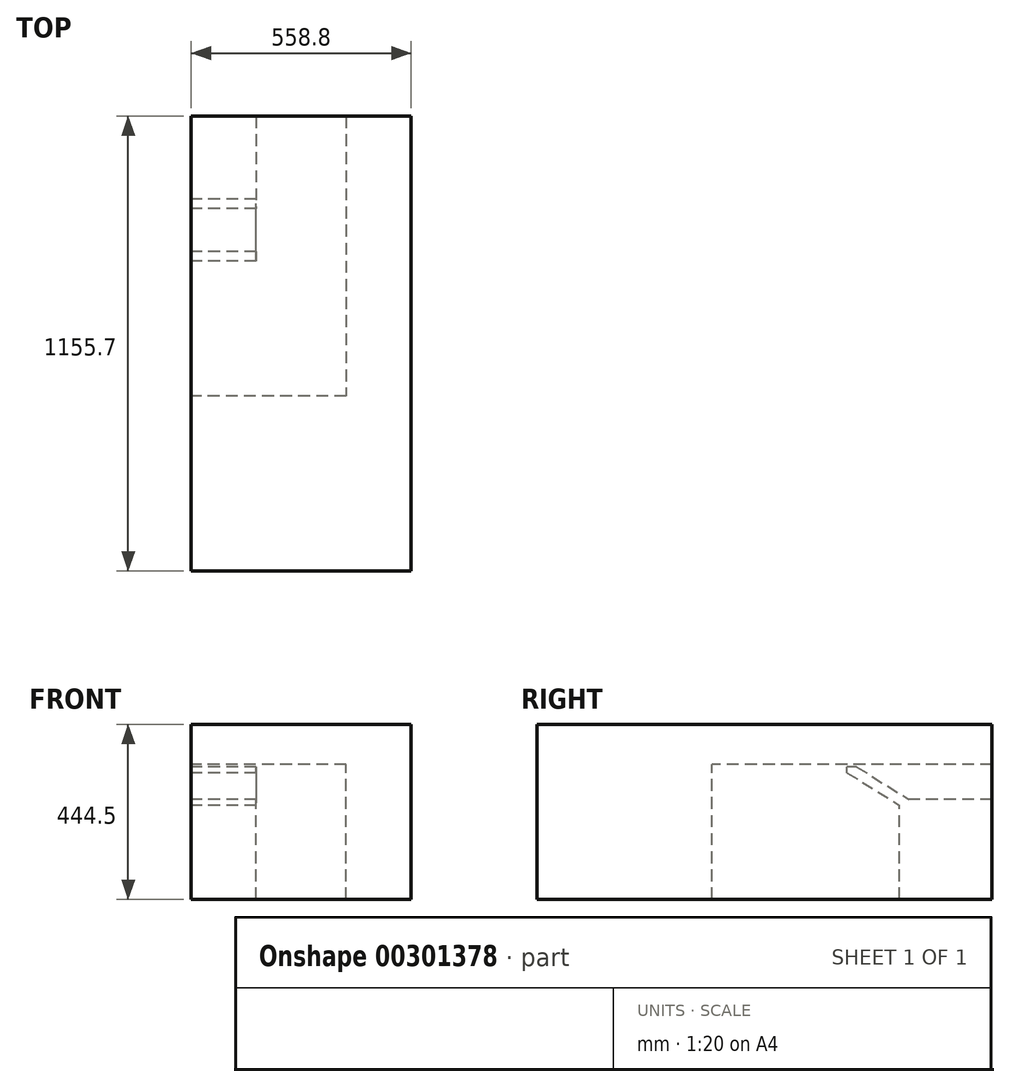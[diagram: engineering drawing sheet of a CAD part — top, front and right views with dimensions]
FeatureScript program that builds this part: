
annotation { "Feature Type Name" : "Feature", "Feature Type Description" : "" }
export const myFeature = defineFeature(function(context is Context, id is Id, definition is map)
    precondition{}
    {
        {
            var Q0;
            Q0=qCreatedBy(makeId("Right.planeOp"),FACE);
            var sketch = newSketch(context, id + "F0", { "sketchPlane" : qUnion([Q0])});
            skLineSegment(sketch, "E0.bottom", {"start": v(0, 0) * mm, "end": v(-1155.7, 0) * mm});
            skLineSegment(sketch, "E0.top", {"start": v(0, 444.5) * mm, "end": v(-1155.7, 444.5) * mm});
            skLineSegment(sketch, "E0.left", {"start": v(0, 0) * mm, "end": v(0, 444.5) * mm});
            skLineSegment(sketch, "E0.right", {"start": v(-1155.7, 0) * mm, "end": v(-1155.7, 444.5) * mm});
            skSolve(sketch);
        }
        {
            var Q0;
            Q0 = qSketchRegion(id + "F0", true);
            extrude(context, id + "F1", {"entities" : qUnion([Q0]), "depth" : 558.8 * mm});
        }
        {
            var Q0;
            Q0=qCreatedBy(makeId("Right.planeOp"),FACE);
            var sketch = newSketch(context, id + "F2", { "sketchPlane" : qUnion([Q0])});
            skLineSegment(sketch, "E1.bottom", {"start": v(0, 0) * mm, "end": v(-711.2, 0) * mm});
            skLineSegment(sketch, "E1.top", {"start": v(0, 342.9) * mm, "end": v(-711.2, 342.9) * mm});
            skLineSegment(sketch, "E1.left", {"start": v(0, 0) * mm, "end": v(0, 342.9) * mm});
            skLineSegment(sketch, "E1.right", {"start": v(-711.2, 0) * mm, "end": v(-711.2, 342.9) * mm});
            skSolve(sketch);
        }
        {
            var Q0;
            Q0 = qSketchRegion(id + "F2", true);
            extrude(context, id + "F3", {"entities" : qUnion([Q0]), "depth" : 393.7 * mm});
        }
        {
            var Q0;
            Q0=qCreatedBy(makeId("Right.planeOp"),FACE);
            var sketch = newSketch(context, id + "F4", { "sketchPlane" : qUnion([Q0])});
            skLineSegment(sketch, "E2.bottom", {"start": v(0, 0) * mm, "end": v(-234.95, 0) * mm});
            skLineSegment(sketch, "E2.top", {"start": v(0, 254) * mm, "end": v(-210.82, 254) * mm});
            skLineSegment(sketch, "E2.left", {"start": v(0, 0) * mm, "end": v(0, 254) * mm});
            skLineSegment(sketch, "E2.right", {"start": v(-234.95, 0) * mm, "end": v(-234.95, 239.06) * mm});
            skLineSegment(sketch, "E3.top", {"start": v(-344.17, 336.55) * mm, "end": v(-368.3, 336.55) * mm});
            skLineSegment(sketch, "E3.right", {"start": v(-368.3, 321.61) * mm, "end": v(-368.3, 336.55) * mm});
            skLineSegment(sketch, "E4.0", {"start": v(-368.3, 321.61) * mm, "end": v(-234.95, 239.06) * mm});
            skLineSegment(sketch, "E5.MirrorCS", {"start": v(-344.17, 336.55) * mm, "end": v(-210.82, 254) * mm});
            skSolve(sketch);
        }
        {
            var Q0;
            Q0 = qSketchRegion(id + "F4", true);
            extrude(context, id + "F5", {"entities" : qUnion([Q0]), "depth" : 165.1 * mm});
        }
    });
